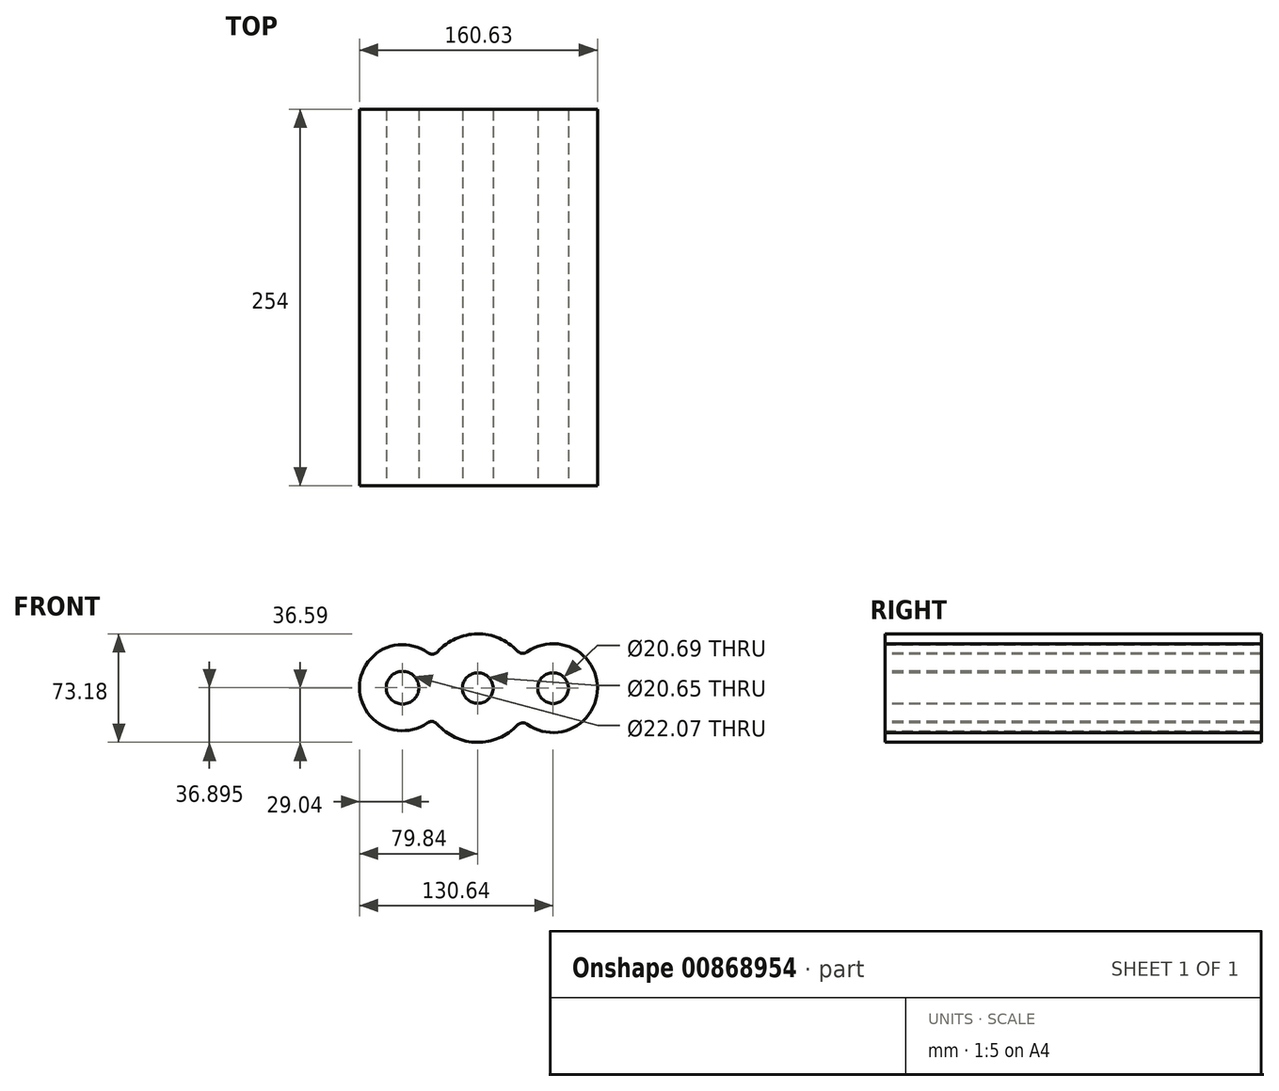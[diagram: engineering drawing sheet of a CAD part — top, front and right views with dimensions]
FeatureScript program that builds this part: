
annotation { "Feature Type Name" : "Feature", "Feature Type Description" : "" }
export const myFeature = defineFeature(function(context is Context, id is Id, definition is map)
    precondition{}
    {
        {
            var Q0;
            Q0=qCreatedBy(makeId("Front.planeOp"),FACE);
            var sketch = newSketch(context, id + "F0", { "sketchPlane" : qUnion([Q0])});
            skLineSegment(sketch, "E0", {"start": v(-65.98, 0) * mm, "end": v(67.85, 0) * mm, "construction": true});
            skLineSegment(sketch, "E1", {"start": v(-50.8, 28.5) * mm, "end": v(-50.8, -22.3) * mm, "construction": true});
            skLineSegment(sketch, "E2", {"start": v(50.8, 28.03) * mm, "end": v(50.8, -22.77) * mm, "construction": true});
            skCircle(sketch, "E3", {"center": v(-50.8, 0.3) * mm, "radius": 29.04 * mm});
            skCircle(sketch, "E4", {"center": v(50.8, 0) * mm, "radius": 30 * mm});
            skCircle(sketch, "E5", {"center": v(0, 0) * mm, "radius": 36.6 * mm});
            skSolve(sketch);
        }
        {
            var Q0;
            Q0 = qSketchRegion(id + "F0", true);
            extrude(context, id + "F1", {"entities" : qUnion([Q0]), "depth" : 254 * mm, "offsetDistance" : 25.4 * mm});
        }
        {
            var Q0;
            {var subQ0=sQuery(id+"F0.wireOp",EDGE,"E5");var subQ1=sQuery(id+"F0.wireOp",EDGE,"E4");Q0=makeQuery(id+"F1.opExtrude","SWEPT_EDGE",EDGE,{"disambiguationData":[OSD([subQ1,subQ0]),TDD([makeQuery(id+"F0.imprint","INTERSECT",VERTEX,{"disambiguationData":[OD(0.0)],"derivedFrom":[subQ1,subQ0]})])]});}
            var Q1;
            {var subQ0=sQuery(id+"F0.wireOp",EDGE,"E5");var subQ1=sQuery(id+"F0.wireOp",EDGE,"E3");Q1=makeQuery(id+"F1.opExtrude","SWEPT_EDGE",EDGE,{"disambiguationData":[OSD([subQ1,subQ0]),TDD([makeQuery(id+"F0.imprint","INTERSECT",VERTEX,{"disambiguationData":[OD(0.0)],"derivedFrom":[subQ1,subQ0]})])]});}
            var Q2;
            {var subQ0=sQuery(id+"F0.wireOp",EDGE,"E5");var subQ1=sQuery(id+"F0.wireOp",EDGE,"E4");Q2=makeQuery(id+"F1.opExtrude","SWEPT_EDGE",EDGE,{"disambiguationData":[OSD([subQ1,subQ0]),TDD([makeQuery(id+"F0.imprint","INTERSECT",VERTEX,{"disambiguationData":[OD(1.0)],"derivedFrom":[subQ1,subQ0]})])]});}
            var Q3;
            {var subQ0=sQuery(id+"F0.wireOp",EDGE,"E5");var subQ1=sQuery(id+"F0.wireOp",EDGE,"E3");Q3=makeQuery(id+"F1.opExtrude","SWEPT_EDGE",EDGE,{"disambiguationData":[OSD([subQ1,subQ0]),TDD([makeQuery(id+"F0.imprint","INTERSECT",VERTEX,{"disambiguationData":[OD(1.0)],"derivedFrom":[subQ1,subQ0]})])]});}
            fillet(context, id + "F2", {"entities" : qUnion([Q0, Q1, Q2, Q3]), "radius" : 5.08 * mm, "tangentPropagation" : true, "allowEdgeOverflow" : false});
        }
        {
            var Q0;
            Q0=makeQuery(id+"F1.opExtrude","CAP_FACE",FACE,{"disambiguationData":[OSD([sQuery(id+"F0.wireOp",EDGE,"E3"),sQuery(id+"F0.wireOp",EDGE,"E4"),sQuery(id+"F0.wireOp",EDGE,"E5")])],"isStart":false});
            var sketch = newSketch(context, id + "F3", { "sketchPlane" : qUnion([Q0])});
            skLineSegment(sketch, "E6", {"start": v(-79.84, 0.13) * mm, "end": v(80.8, 0.13) * mm, "construction": true});
            skPoint(sketch, "E6.startSnap0", {"position": v(-79.84, 0.48) * mm});
            skCircle(sketch, "E7", {"center": v(-50.8, 0.3) * mm, "radius": 11.03 * mm});
            skCircle(sketch, "E8", {"center": v(0, 0) * mm, "radius": 10.32 * mm});
            skCircle(sketch, "E9", {"center": v(50.8, 0) * mm, "radius": 10.34 * mm});
            skSolve(sketch);
        }
        {
            var Q0;
            Q0=makeQuery(id+"F3.imprint","IMPRINT",FACE,{"disambiguationData":[TD([[makeQuery(id+"F3.imprint","IMPRINT",EDGE,{"derivedFrom":sQuery(id+"F3.wireOp",EDGE,"E7")}),1.0]])]});
            var Q1;
            Q1=makeQuery(id+"F3.imprint","IMPRINT",FACE,{"disambiguationData":[TD([[makeQuery(id+"F3.imprint","IMPRINT",EDGE,{"derivedFrom":sQuery(id+"F3.wireOp",EDGE,"E8")}),1.0]])]});
            var Q2;
            Q2=makeQuery(id+"F3.imprint","IMPRINT",FACE,{"disambiguationData":[TD([[makeQuery(id+"F3.imprint","IMPRINT",EDGE,{"derivedFrom":sQuery(id+"F3.wireOp",EDGE,"E9")}),1.0]])]});
            extrude(context, id + "F4", {"entities" : qUnion([Q0, Q1, Q2]), "operationType" : NewBodyOperationType.REMOVE, "oppositeDirection" : true, "depth" : 461.26 * mm, "offsetDistance" : 25.4 * mm});
        }
        {
            var Q0;
            Q0=qCreatedBy(makeId("Top.planeOp"),FACE);
            var sketch = newSketch(context, id + "F5", { "sketchPlane" : qUnion([Q0])});
            skLineSegment(sketch, "E10", {"start": v(0, 0) * mm, "end": v(0, -254.43) * mm, "construction": true});
            skLineSegment(sketch, "E11", {"start": v(0, -127.22) * mm, "end": v(-195.56, -127.22) * mm, "construction": true});
            skCircle(sketch, "E12", {"center": v(-75.88, -127.22) * mm, "radius": 24.18 * mm});
            skSolve(sketch);
        }
        {
            var Q0;
            Q0=sQuery(id+"F5.wireOp",EDGE,"E12");
            extrude(context, id + "F6", {"bodyType" : ToolBodyType.SURFACE, "operationType" : NewBodyOperationType.INTERSECT, "surfaceEntities" : qUnion([Q0]), "depth" : 110.74 * mm, "offsetDistance" : 25.4 * mm, "hasSecondDirection" : true, "secondDirectionOppositeDirection" : true, "secondDirectionDepth" : 70.61 * mm});
        }
    });
